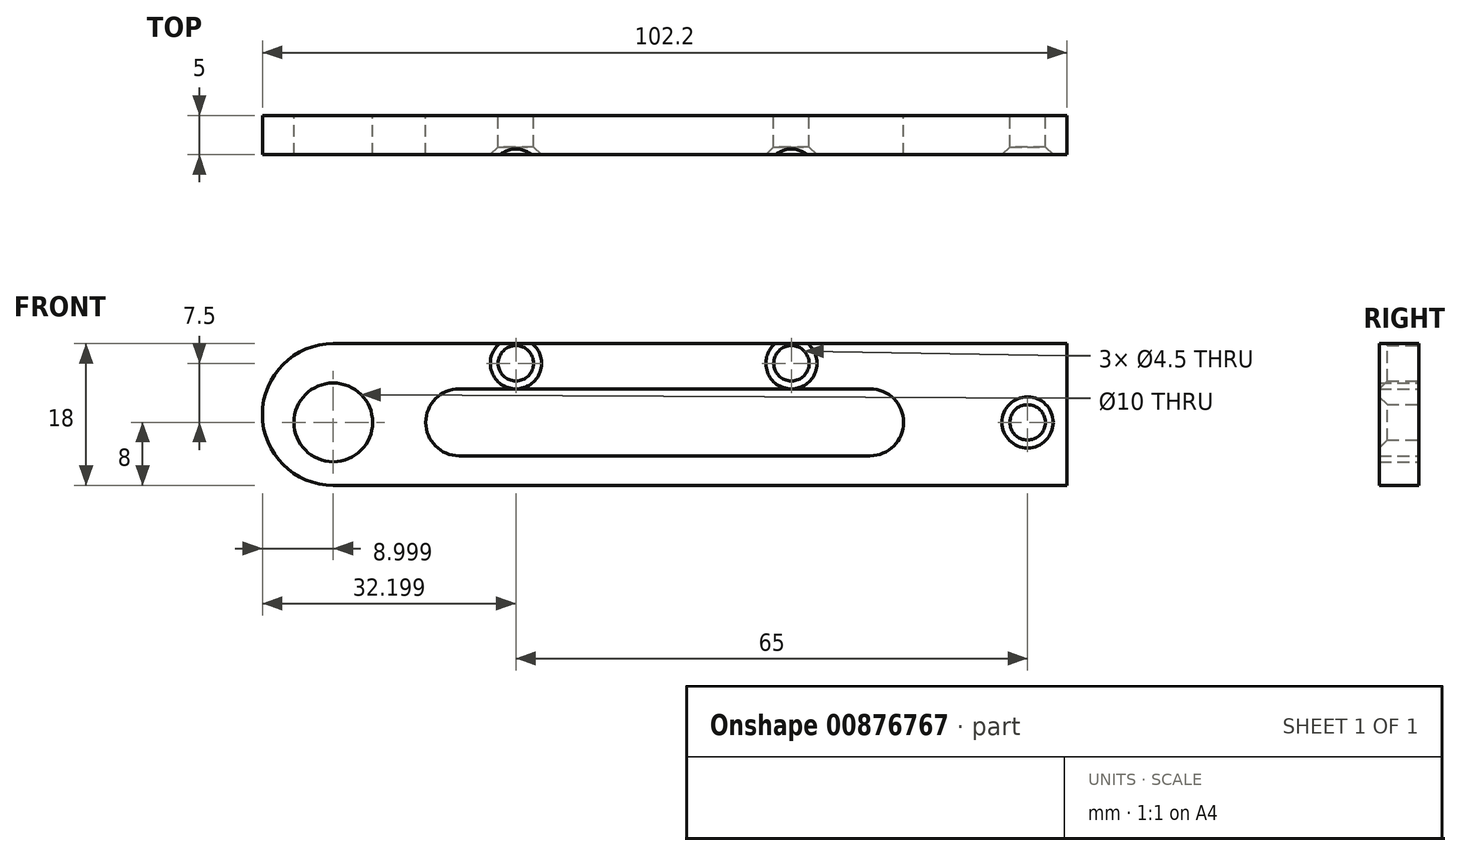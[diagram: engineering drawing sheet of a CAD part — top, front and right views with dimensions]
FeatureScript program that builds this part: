
annotation { "Feature Type Name" : "Feature", "Feature Type Description" : "" }
export const myFeature = defineFeature(function(context is Context, id is Id, definition is map)
    precondition{}
    {
        {
            var Q0;
            Q0=qCreatedBy(makeId("Front.planeOp"),FACE);
            var sketch = newSketch(context, id + "F0", { "sketchPlane" : qUnion([Q0])});
            skCircle(sketch, "E0", {"center": v(-38.63, 0) * mm, "radius": 5 * mm});
            skPoint(sketch, "E1", {"position": v(-22.63, 0) * mm});
            skPoint(sketch, "E2", {"position": v(29.57, 0) * mm});
            skPoint(sketch, "E3.middle", {"position": v(0, 0) * mm});
            skPoint(sketch, "E4", {"position": v(-38.63, 10) * mm});
            skPoint(sketch, "E5", {"position": v(-38.63, -8) * mm});
            skArc(sketch, "E6", {"start": v(-38.63, 10) * mm, "mid": v(-47.63, 1) * mm, "end": v(-38.63, -8) * mm});
            skLineSegment(sketch, "E7.right", {"start": v(54.57, 10) * mm, "end": v(54.57, -8) * mm});
            skLineSegment(sketch, "E8", {"start": v(-38.63, 10) * mm, "end": v(54.57, 10) * mm});
            skLineSegment(sketch, "E9", {"start": v(-38.63, -8) * mm, "end": v(54.57, -8) * mm});
            skCircle(sketch, "E10", {"center": v(49.57, 0) * mm, "radius": 2.25 * mm});
            skCircle(sketch, "E11", {"center": v(19.57, 7.5) * mm, "radius": 2.25 * mm});
            skCircle(sketch, "E12", {"center": v(-15.43, 7.5) * mm, "radius": 2.25 * mm});
            skArc(sketch, "E13", {"start": v(-22.63, 4.25) * mm, "mid": v(-26.88, 0) * mm, "end": v(-22.63, -4.25) * mm});
            skArc(sketch, "E14", {"start": v(29.57, -4.25) * mm, "mid": v(33.82, 0) * mm, "end": v(29.57, 4.25) * mm});
            skLineSegment(sketch, "E15.top", {"start": v(-22.63, 4.25) * mm, "end": v(29.57, 4.25) * mm});
            skLineSegment(sketch, "E16.top", {"start": v(-22.63, -4.25) * mm, "end": v(29.57, -4.25) * mm});
            skSolve(sketch);
        }
        {
            var Q0;
            Q0=qSketchRegion(id+"F0",true);
            extrude(context, id + "F1", {"entities" : qUnion([Q0]), "depth" : 5 * mm, "offsetDistance" : 25 * mm});
        }
        {
            var Q0;
            Q0=makeQuery(id+"F1.opExtrude","CAP_EDGE",EDGE,{"disambiguationData":[OSD([sQuery(id+"F0.wireOp",EDGE,"E12")])],"isStart":false});
            var Q1;
            Q1=makeQuery(id+"F1.opExtrude","CAP_EDGE",EDGE,{"disambiguationData":[OSD([sQuery(id+"F0.wireOp",EDGE,"E11")])],"isStart":false});
            var Q2;
            Q2=makeQuery(id+"F1.opExtrude","CAP_EDGE",EDGE,{"disambiguationData":[OSD([sQuery(id+"F0.wireOp",EDGE,"E10")])],"isStart":false});
            chamfer(context, id + "F2", {"entities" : qUnion([Q0, Q1, Q2]), "width" : 1 * mm, "tangentPropagation" : true});
        }
    });
